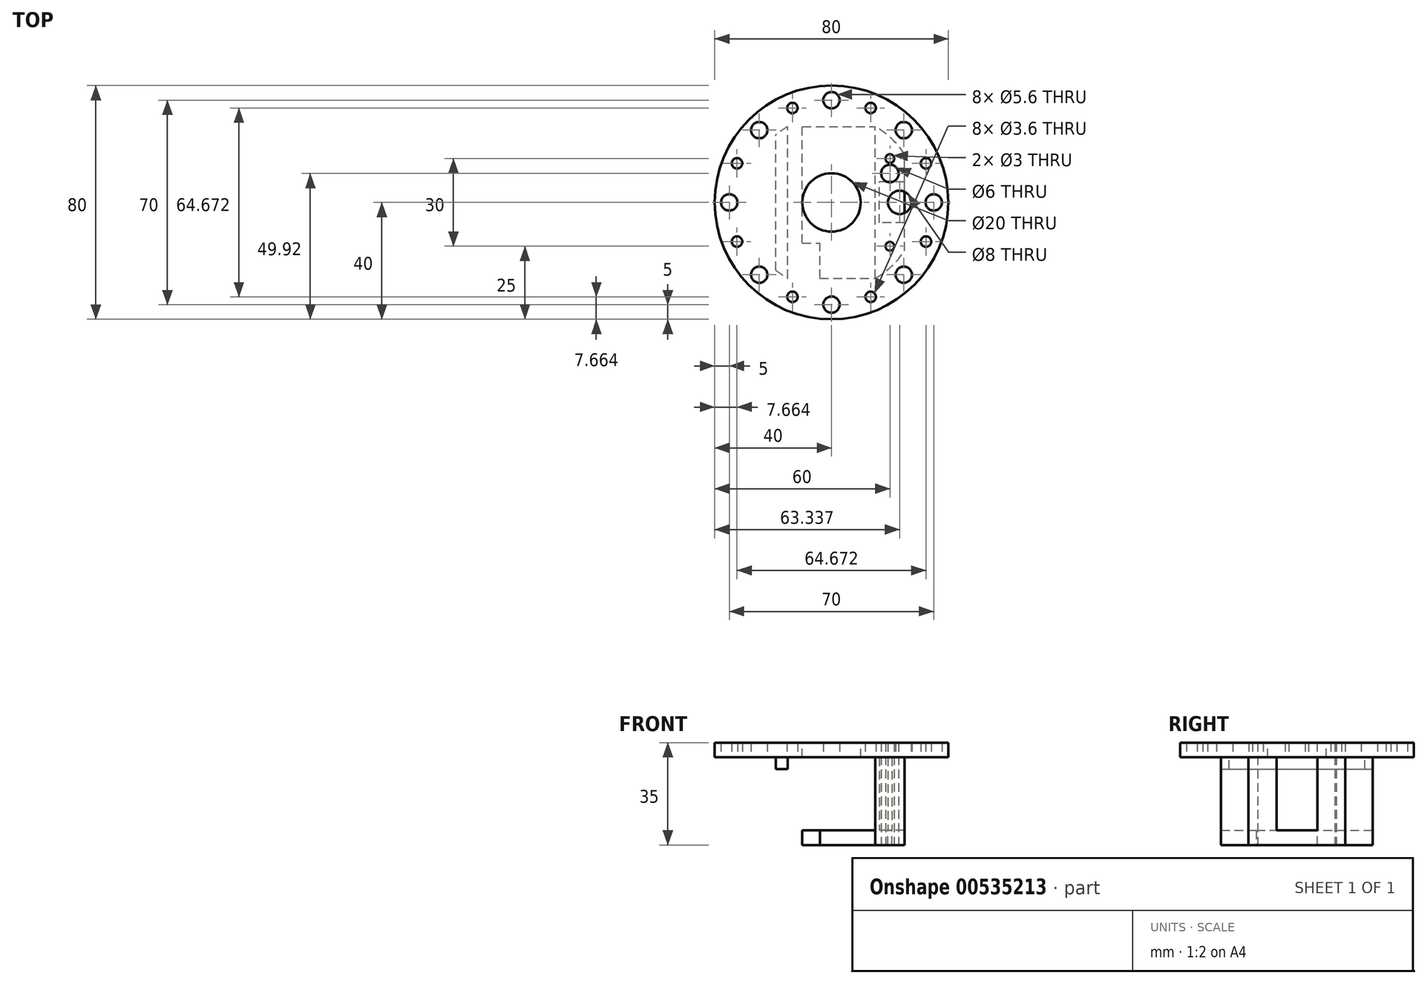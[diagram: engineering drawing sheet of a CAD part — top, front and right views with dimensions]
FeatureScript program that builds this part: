
annotation { "Feature Type Name" : "Feature", "Feature Type Description" : "" }
export const myFeature = defineFeature(function(context is Context, id is Id, definition is map)
    precondition{}
    {
        {
            var Q0;
            Q0=qCreatedBy(makeId("Top.planeOp"),FACE);
            var sketch = newSketch(context, id + "F0", { "sketchPlane" : qUnion([Q0])});
            skCircle(sketch, "E0", {"center": v(0, 0) * mm, "radius": 10 * mm});
            skCircle(sketch, "E1", {"center": v(0, 0) * mm, "radius": 40 * mm});
            skSolve(sketch);
        }
        {
            var Q0;
            Q0=makeQuery(id+"F0.imprint","IMPRINT",FACE,{"disambiguationData":[TD([[makeQuery(id+"F0.imprint","IMPRINT",EDGE,{"derivedFrom":sQuery(id+"F0.wireOp",EDGE,"E0")}),-1.0]])]});
            extrude(context, id + "F1", {"entities" : qUnion([Q0]), "oppositeDirection" : true, "depth" : 5 * mm, "offsetDistance" : 25 * mm});
        }
        {
            var Q0;
            Q0=makeQuery(id+"F1.opExtrude","CAP_FACE",FACE,{"disambiguationData":[OSD([sQuery(id+"F0.wireOp",EDGE,"E0"),sQuery(id+"F0.wireOp",EDGE,"E1")])],"isStart":false});
            var sketch = newSketch(context, id + "F2", { "sketchPlane" : qUnion([Q0])});
            skLineSegment(sketch, "E2", {"start": v(-15, 0) * mm, "end": v(15, 0) * mm, "construction": true});
            skLineSegment(sketch, "E3.bottom", {"start": v(-15, 37.08) * mm, "end": v(-25, 37.08) * mm});
            skLineSegment(sketch, "E3.top", {"start": v(-15, -37.08) * mm, "end": v(-25, -37.08) * mm});
            skLineSegment(sketch, "E3.left", {"start": v(-15, 37.08) * mm, "end": v(-15, -37.08) * mm});
            skLineSegment(sketch, "E3.right", {"start": v(-25, 37.08) * mm, "end": v(-25, -37.08) * mm});
            skLineSegment(sketch, "E4", {"start": v(0, 21.18) * mm, "end": v(0, -25.4) * mm, "construction": true});
            skLineSegment(sketch, "E5.MirrorCS", {"start": v(25, 37.08) * mm, "end": v(25, -37.08) * mm});
            skLineSegment(sketch, "E6.MirrorCS", {"start": v(15, 37.08) * mm, "end": v(25, 37.08) * mm});
            skLineSegment(sketch, "E7.MirrorCS", {"start": v(15, 37.08) * mm, "end": v(15, -37.08) * mm});
            skLineSegment(sketch, "E8.MirrorCS", {"start": v(15, -37.08) * mm, "end": v(25, -37.08) * mm});
            skCircle(sketch, "E9", {"center": v(0, 0) * mm, "radius": 30 * mm});
            skLineSegment(sketch, "E10", {"start": v(-15, 0) * mm, "end": v(-19, 0) * mm, "construction": true});
            skLineSegment(sketch, "E11", {"start": v(-19, 23.22) * mm, "end": v(-19, -23.22) * mm});
            skSolve(sketch);
        }
        {
            var Q0;
            {var subQ0=sQuery(id+"F2.wireOp",EDGE,"E9");var subQ1=sQuery(id+"F2.wireOp",EDGE,"E3.left");var subQ2=makeQuery(id+"F2.imprint","INTERSECT",VERTEX,{"disambiguationData":[OD(0.0)],"derivedFrom":[subQ1,subQ0]});Q0=makeQuery(id+"F2.imprint","IMPRINT",FACE,{"disambiguationData":[TD([[makeQuery(id+"F2.imprint","IMPRINT",EDGE,{"disambiguationData":[TD([[subQ2,-1.0]])],"derivedFrom":subQ1}),-1.0]])]});}
            extrude(context, id + "F3", {"entities" : qUnion([Q0]), "operationType" : NewBodyOperationType.ADD, "depth" : 4 * mm, "offsetDistance" : 25 * mm});
        }
        {
            var Q0;
            {var subQ0=sQuery(id+"F2.wireOp",EDGE,"E9");var subQ1=sQuery(id+"F2.wireOp",EDGE,"E5.MirrorCS");var subQ2=makeQuery(id+"F2.imprint","INTERSECT",VERTEX,{"disambiguationData":[OD(0.0)],"derivedFrom":[subQ1,subQ0]});Q0=makeQuery(id+"F2.imprint","IMPRINT",FACE,{"disambiguationData":[TD([[makeQuery(id+"F2.imprint","IMPRINT",EDGE,{"disambiguationData":[TD([[subQ2,-1.0]])],"derivedFrom":subQ1}),-1.0]])]});}
            extrude(context, id + "F4", {"entities" : qUnion([Q0]), "operationType" : NewBodyOperationType.ADD, "depth" : 25 * mm, "offsetDistance" : 25 * mm});
        }
        {
            var Q0;
            Q0=makeQuery(id+"F4.opExtrude","CAP_FACE",FACE,{"disambiguationData":[OSD([sQuery(id+"F0.wireOp",EDGE,"E1"),sQuery(id+"F2.wireOp",EDGE,"E5.MirrorCS"),sQuery(id+"F2.wireOp",EDGE,"E7.MirrorCS")])],"isStart":false});
            var sketch = newSketch(context, id + "F5", { "sketchPlane" : qUnion([Q0])});
            skLineSegment(sketch, "E12", {"start": v(25, 0) * mm, "end": v(15, 0) * mm, "construction": true});
            skLineSegment(sketch, "E13", {"start": v(20, 15) * mm, "end": v(20, -15) * mm});
            skPoint(sketch, "E13.startSnap0", {"position": v(20, 0) * mm});
            skCircle(sketch, "E14", {"center": v(20, 15) * mm, "radius": 1.5 * mm});
            skCircle(sketch, "E15", {"center": v(20, -15) * mm, "radius": 1.5 * mm});
            skCircle(sketch, "E16", {"center": v(20, -9.92) * mm, "radius": 3 * mm});
            skSolve(sketch);
        }
        {
            var Q0;
            Q0 = qSketchRegion(id + "F5", true);
            extrude(context, id + "F6", {"entities" : qUnion([Q0]), "operationType" : NewBodyOperationType.REMOVE, "oppositeDirection" : true, "depth" : 30.7 * mm, "offsetDistance" : 25 * mm});
        }
        {
            var Q0;
            Q0=makeQuery(id+"F1.opExtrude","CAP_FACE",FACE,{"disambiguationData":[OSD([sQuery(id+"F0.wireOp",EDGE,"E0"),sQuery(id+"F0.wireOp",EDGE,"E1")])],"isStart":false});
            var sketch = newSketch(context, id + "F7", { "sketchPlane" : qUnion([Q0])});
            skLineSegment(sketch, "E17", {"start": v(0, 40) * mm, "end": v(0, -40) * mm, "construction": true});
            skLineSegment(sketch, "E18", {"start": v(-40, 0) * mm, "end": v(40, 0) * mm, "construction": true});
            skCircle(sketch, "E19", {"center": v(0, 0) * mm, "radius": 35 * mm, "construction": true});
            skCircle(sketch, "E20", {"center": v(0, 35) * mm, "radius": 2.8 * mm});
            skCircle(sketch, "E21.1.0", {"center": v(-24.75, 24.75) * mm, "radius": 2.8 * mm});
            skCircle(sketch, "E21.2.0", {"center": v(-35, 0) * mm, "radius": 2.8 * mm});
            skCircle(sketch, "E21.3.0", {"center": v(-24.75, -24.75) * mm, "radius": 2.8 * mm});
            skCircle(sketch, "E22.1.4.0", {"center": v(0, -35) * mm, "radius": 2.8 * mm});
            skCircle(sketch, "E22.1.5.0", {"center": v(24.75, -24.75) * mm, "radius": 2.8 * mm});
            skCircle(sketch, "E22.1.6.0", {"center": v(35, 0) * mm, "radius": 2.8 * mm});
            skCircle(sketch, "E22.1.7.0", {"center": v(24.75, 24.75) * mm, "radius": 2.8 * mm});
            skSolve(sketch);
        }
        {
            var Q0;
            Q0 = qSketchRegion(id + "F7", true);
            extrude(context, id + "F8", {"entities" : qUnion([Q0]), "operationType" : NewBodyOperationType.REMOVE, "oppositeDirection" : true, "depth" : 25 * mm, "offsetDistance" : 25 * mm});
        }
        {
            var Q0;
            Q0=makeQuery(id+"F1.opExtrude","CAP_FACE",FACE,{"disambiguationData":[OSD([sQuery(id+"F0.wireOp",EDGE,"E0"),sQuery(id+"F0.wireOp",EDGE,"E1")])],"isStart":false});
            var sketch = newSketch(context, id + "F9", { "sketchPlane" : qUnion([Q0])});
            skLineSegment(sketch, "E23", {"start": v(0, 35) * mm, "end": v(24.75, 24.75) * mm, "construction": true});
            skCircle(sketch, "E24", {"center": v(0, 0) * mm, "radius": 35 * mm, "construction": true});
            skPoint(sketch, "E25", {"position": v(12.37, 29.87) * mm});
            skLineSegment(sketch, "E26", {"start": v(0, 0) * mm, "end": v(15.3, 36.96) * mm});
            skCircle(sketch, "E27", {"center": v(13.4, 32.34) * mm, "radius": 1.8 * mm});
            skCircle(sketch, "E28.1.0", {"center": v(-13.4, 32.34) * mm, "radius": 1.8 * mm});
            skCircle(sketch, "E28.2.0", {"center": v(-32.34, 13.4) * mm, "radius": 1.8 * mm});
            skCircle(sketch, "E28.3.0", {"center": v(-32.34, -13.4) * mm, "radius": 1.8 * mm});
            skCircle(sketch, "E28.4.0", {"center": v(-13.4, -32.34) * mm, "radius": 1.8 * mm});
            skCircle(sketch, "E28.5.0", {"center": v(13.4, -32.34) * mm, "radius": 1.8 * mm});
            skCircle(sketch, "E28.6.0", {"center": v(32.34, -13.4) * mm, "radius": 1.8 * mm});
            skCircle(sketch, "E28.7.0", {"center": v(32.34, 13.4) * mm, "radius": 1.8 * mm});
            skSolve(sketch);
        }
        {
            var Q0;
            Q0 = qSketchRegion(id + "F9", true);
            extrude(context, id + "F10", {"entities" : qUnion([Q0]), "operationType" : NewBodyOperationType.REMOVE, "oppositeDirection" : true, "depth" : 25 * mm, "offsetDistance" : 25 * mm});
        }
        {
            var Q0;
            Q0=makeQuery(id+"F1.opExtrude","CAP_FACE",FACE,{"disambiguationData":[OSD([sQuery(id+"F0.wireOp",EDGE,"E0"),sQuery(id+"F0.wireOp",EDGE,"E1")])],"isStart":false});
            var sketch = newSketch(context, id + "F11", { "sketchPlane" : qUnion([Q0])});
            skLineSegment(sketch, "E29", {"start": v(0, 0) * mm, "end": v(40, 0) * mm});
            skCircle(sketch, "E30", {"center": v(23.34, 0) * mm, "radius": 4 * mm});
            skPoint(sketch, "E31", {"position": v(25, 0) * mm});
            skSolve(sketch);
        }
        {
            var Q0;
            Q0 = qSketchRegion(id + "F11", true);
            extrude(context, id + "F12", {"entities" : qUnion([Q0]), "operationType" : NewBodyOperationType.REMOVE, "oppositeDirection" : true, "depth" : 25 * mm, "offsetDistance" : 25 * mm});
        }
        {
            var Q0;
            Q0=makeQuery(id+"F4.opExtrude","CAP_FACE",FACE,{"disambiguationData":[OSD([sQuery(id+"F2.wireOp",EDGE,"E5.MirrorCS"),sQuery(id+"F2.wireOp",EDGE,"E7.MirrorCS"),sQuery(id+"F2.wireOp",EDGE,"E9")])],"isStart":false});
            var sketch = newSketch(context, id + "F13", { "sketchPlane" : qUnion([Q0])});
            skArc(sketch, "E32.0", {"start": v(25, -3.64) * mm, "mid": v(27.34, 0) * mm, "end": v(25, 3.64) * mm, "construction": true});
            skLineSegment(sketch, "E33.bottom", {"start": v(30.34, 7) * mm, "end": v(16.34, 7) * mm});
            skLineSegment(sketch, "E33.top", {"start": v(30.34, -7) * mm, "end": v(16.34, -7) * mm});
            skLineSegment(sketch, "E33.left", {"start": v(30.34, 7) * mm, "end": v(30.34, -7) * mm});
            skLineSegment(sketch, "E33.right", {"start": v(16.34, 7) * mm, "end": v(16.34, -7) * mm});
            skSolve(sketch);
        }
        {
            var Q0;
            Q0 = qSketchRegion(id + "F13", true);
            extrude(context, id + "F14", {"entities" : qUnion([Q0]), "operationType" : NewBodyOperationType.REMOVE, "oppositeDirection" : true, "depth" : 25 * mm, "offsetDistance" : 25 * mm});
        }
        {
            var Q0;
            Q0=makeQuery(id+"F4.opExtrude","CAP_FACE",FACE,{"disambiguationData":[OSD([sQuery(id+"F2.wireOp",EDGE,"E5.MirrorCS"),sQuery(id+"F2.wireOp",EDGE,"E7.MirrorCS"),sQuery(id+"F2.wireOp",EDGE,"E9")])],"isStart":false});
            var sketch = newSketch(context, id + "F15", { "sketchPlane" : qUnion([Q0])});
            skLineSegment(sketch, "E34.0", {"start": v(15, 25.98) * mm, "end": v(15, -25.98) * mm});
            skArc(sketch, "E34.1", {"start": v(25, 16.58) * mm, "mid": v(20.54, 21.86) * mm, "end": v(15, 25.98) * mm});
            skLineSegment(sketch, "E34.2", {"start": v(25, 16.58) * mm, "end": v(25, 7) * mm});
            skLineSegment(sketch, "E34.3", {"start": v(25, -7) * mm, "end": v(25, -16.58) * mm});
            skArc(sketch, "E34.4", {"start": v(15, -25.98) * mm, "mid": v(20.54, -21.86) * mm, "end": v(25, -16.58) * mm});
            skLineSegment(sketch, "E35", {"start": v(25, 7) * mm, "end": v(25, -7) * mm});
            skCircle(sketch, "E36.0", {"center": v(20, 15) * mm, "radius": 1.5 * mm});
            skArc(sketch, "E36.1", {"start": v(19.31, -7) * mm, "mid": v(20, -12.92) * mm, "end": v(20.69, -7) * mm});
            skCircle(sketch, "E36.2", {"center": v(20, -15) * mm, "radius": 1.5 * mm});
            skLineSegment(sketch, "E37", {"start": v(19.31, -7) * mm, "end": v(20.69, -7) * mm});
            skSolve(sketch);
        }
        {
            var Q0;
            Q0 = qSketchRegion(id + "F15", true);
            extrude(context, id + "F16", {"entities" : qUnion([Q0]), "depth" : 5 * mm, "offsetDistance" : 25 * mm});
        }
        {
            var Q0;
            Q0=makeQuery(id+"F16.opExtrude","SWEPT_FACE",FACE,{"disambiguationData":[OSD([sQuery(id+"F15.wireOp",EDGE,"E34.0")])]});
            extrude(context, id + "F17", {"entities" : qUnion([Q0]), "operationType" : NewBodyOperationType.ADD, "depth" : 25 * mm, "offsetDistance" : 25 * mm});
        }
        {
            var Q0;
            {var subQ0=sQuery(id+"F15.wireOp",EDGE,"E34.0");Q0=makeQuery(id+"F17.boolean.opBoolean","MERGE",FACE,{"derivedFrom":[makeQuery(id+"F16.opExtrude","CAP_FACE",FACE,{"disambiguationData":[OSD([subQ0,sQuery(id+"F15.wireOp",EDGE,"E34.1"),sQuery(id+"F15.wireOp",EDGE,"E34.2"),sQuery(id+"F15.wireOp",EDGE,"E34.3"),sQuery(id+"F15.wireOp",EDGE,"E34.4"),sQuery(id+"F15.wireOp",EDGE,"E35"),sQuery(id+"F15.wireOp",EDGE,"E36.0"),sQuery(id+"F15.wireOp",EDGE,"E36.1"),sQuery(id+"F15.wireOp",EDGE,"E36.2"),sQuery(id+"F15.wireOp",EDGE,"E37")])],"isStart":false}),makeQuery(id+"F17.opExtrude","SWEPT_FACE",FACE,{"disambiguationData":[OSD([subQ0]),TDD([makeQuery(id+"F16.opExtrude","CAP_EDGE",EDGE,{"disambiguationData":[OSD([subQ0])],"isStart":false})])]})]});}
            var sketch = newSketch(context, id + "F18", { "sketchPlane" : qUnion([Q0])});
            skLineSegment(sketch, "E38.bottom", {"start": v(-10, 25.98) * mm, "end": v(-3.98, 25.98) * mm});
            skLineSegment(sketch, "E38.top", {"start": v(-10, 13.94) * mm, "end": v(-3.98, 13.94) * mm});
            skLineSegment(sketch, "E38.left", {"start": v(-10, 25.98) * mm, "end": v(-10, 13.94) * mm});
            skLineSegment(sketch, "E38.right", {"start": v(-3.98, 25.98) * mm, "end": v(-3.98, 13.94) * mm});
            skSolve(sketch);
        }
        {
            var Q0;
            Q0 = qSketchRegion(id + "F18", true);
            extrude(context, id + "F19", {"entities" : qUnion([Q0]), "operationType" : NewBodyOperationType.REMOVE, "oppositeDirection" : true, "depth" : 25 * mm, "offsetDistance" : 25 * mm});
        }
    });
